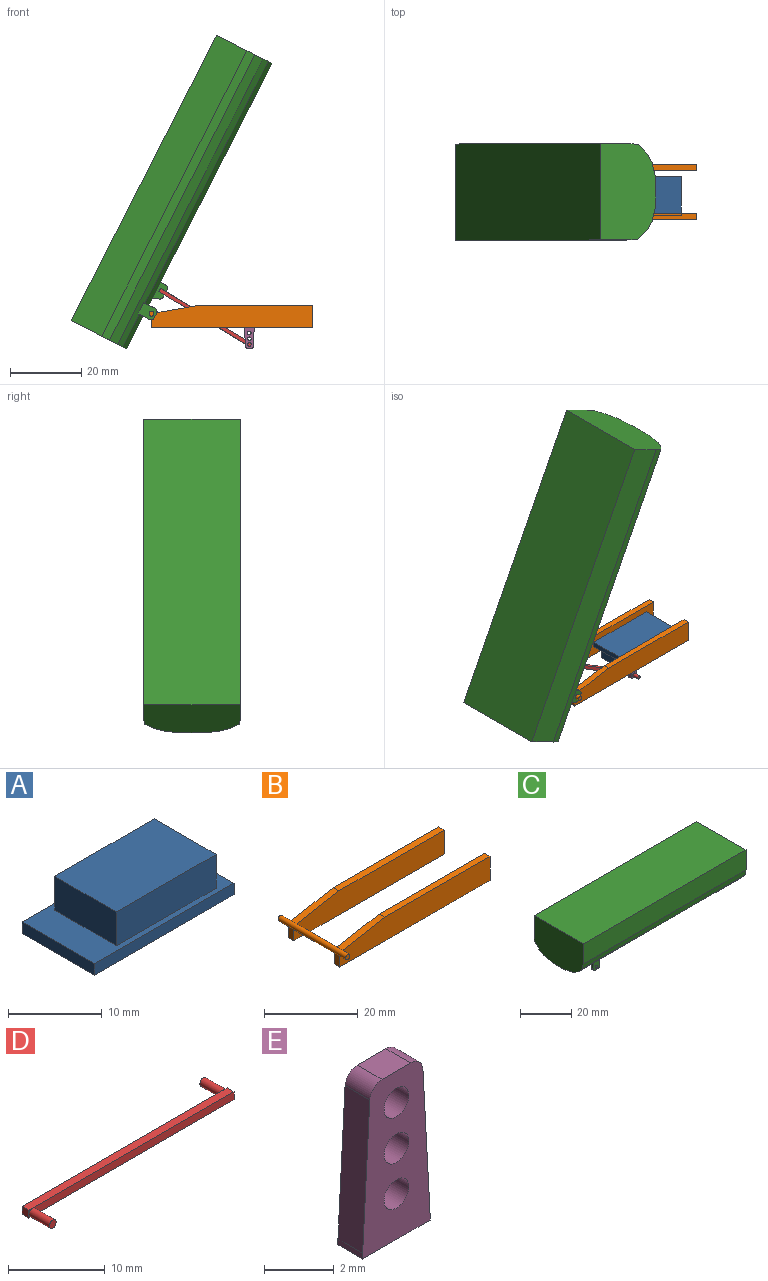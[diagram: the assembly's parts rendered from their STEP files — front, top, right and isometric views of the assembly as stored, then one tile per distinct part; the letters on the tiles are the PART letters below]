
ASSEMBLY  parts=5 mates=5
PART A: 11 faces, bbox 21x10.9x5.9 mm
  f0: plane 21x10.9mm, normal (0,0,1), area 89.4mm2, adj f1,f3,f4,f5,f6,f7,f8,f9
  f1: plane 10.9x1.5mm, normal (-1,0,0), area 16.3mm2, adj f0,f2,f4,f5
  f2: plane 21x10.9mm, normal (0,0,-1), area 228.9mm2, adj f1,f3,f4,f5
  f3: plane 10.9x1.5mm, normal (1,0,0), area 16.3mm2, adj f0,f2,f4,f5
  f4: plane 21x1.5mm, normal (0,1,0), area 31.5mm2, adj f0,f1,f2,f3
  f5: plane 21x1.5mm, normal (0,-1,0), area 31.5mm2, adj f0,f1,f2,f3
  f6: plane 15x4.4mm, normal (0,1,0), area 66mm2, adj f0,f7,f9,f10
  f7: plane 9.3x4.4mm, normal (-1,0,0), area 40.9mm2, adj f0,f6,f8,f10
  f8: plane 15x4.4mm, normal (0,-1,0), area 66mm2, adj f0,f7,f9,f10
  f9: plane 9.3x4.4mm, normal (1,0,0), area 40.9mm2, adj f0,f6,f8,f10
  f10: plane 15x9.3mm, normal (0,0,1), area 139.5mm2, adj f6,f7,f8,f9
PART B: 17 faces, bbox 46.1x20.4x6.3 mm
  f0: plane 3.18x1.7mm, normal (-1,0,0), area 5.4mm2, adj f1,f5,f6,f14
  f1: plane 45.4x1.7mm, normal (0,0,-1), area 77.2mm2, adj f0,f2,f5,f6
  f2: plane 6.25x1.7mm, normal (1,0,0), area 10.6mm2, adj f1,f3,f5,f6
  f3: plane 31.8x1.7mm, normal (0,0,1), area 54.1mm2, adj f2,f4,f5,f6
  f4: plane 12.94x2.28mm, normal (-0.17,0,0.98), area 22.3mm2, adj f3,f5,f6,f14
  f5: plane 45.4x6.25mm, normal (0,-1,0), area 267mm2, adj f0,f1,f2,f3,f4,f14
  f6: plane 45.4x6.25mm, normal (0,1,0), area 267mm2, adj f0,f1,f2,f3,f4,f14
  f7: plane 3.18x1.7mm, normal (-1,0,0), area 5.4mm2, adj f8,f12,f13,f14
  f8: plane 45.4x1.7mm, normal (0,0,-1), area 77.2mm2, adj f7,f9,f12,f13
  f9: plane 6.25x1.7mm, normal (1,0,0), area 10.6mm2, adj f8,f10,f12,f13
  f10: plane 31.8x1.7mm, normal (0,0,1), area 54.1mm2, adj f9,f11,f12,f13
  f11: plane 12.94x2.28mm, normal (-0.17,0,0.98), area 22.3mm2, adj f10,f12,f13,f14
  f12: plane 45.4x6.25mm, normal (0,-1,0), area 267mm2, adj f7,f8,f9,f10,f11,f14
  f13: plane 45.4x6.25mm, normal (0,1,0), area 267mm2, adj f7,f8,f9,f10,f11,f14
  f14: cylinder r=0.68mm len=20.4mm, axis (0,-1,0), area 82.5mm2, adj f0,f4,f5,f6,f7,f11,f12,f13
  f15: plane 1.35x1.35mm, normal (0,1,0), area 1.4mm2, adj f14
  f16: plane 1.35x1.35mm, normal (0,-1,0), area 1.4mm2, adj f14
PART C: 38 faces, bbox 90.1x27.1x20.5 mm
  f0: plane 90.1x7mm, normal (0,0,-1), area 620.7mm2, adj f1,f3,f12,f13,f30,f31,f32,f33
  f1: plane 90.1x4.85mm, normal (0,0.25,-0.97), area 448.7mm2, adj f0,f2,f12,f13,f22,f23,f25
  f2: plane 90.1x2.53mm, normal (0,0.54,-0.84), area 267.4mm2, adj f1,f11,f12,f13,f23,f24,f25
  f3: plane 90.1x4.85mm, normal (0,-0.25,-0.97), area 448.4mm2, adj f0,f4,f12,f13,f15,f16,f17
  f4: plane 90.1x2.53mm, normal (0,-0.54,-0.84), area 267.7mm2, adj f3,f5,f12,f13,f14,f15,f17
  f5: plane 90.1x2.58mm, normal (0,-0.74,-0.67), area 315.3mm2, adj f4,f6,f12,f13
  f6: plane 90.1x2.48mm, normal (0,-0.99,-0.13), area 225.2mm2, adj f5,f7,f12,f13
  f7: plane 90.1x9.6mm, normal (0,-1,0), area 865mm2, adj f6,f8,f12,f13
  f8: plane 90.1x27.13mm, normal (0,0,1), area 2444.4mm2, adj f7,f9,f12,f13
  f9: plane 90.1x9.6mm, normal (0,1,0), area 865mm2, adj f8,f10,f12,f13
  f10: plane 90.1x2.48mm, normal (0,0.99,-0.13), area 225.2mm2, adj f9,f11,f12,f13
  f11: plane 90.1x2.58mm, normal (0,0.74,-0.67), area 315.3mm2, adj f2,f10,f12,f13
  f12: plane 27.13x17.5mm, normal (1,0,0), area 434.7mm2, adj f0,f1,f2,f3,f4,f5,f6,f7
  f13: plane 27.13x17.5mm, normal (-1,0,0), area 434.7mm2, adj f0,f1,f2,f3,f4,f5,f6,f7
  f14: plane 4.62x3.5mm, normal (0,-1,0), area 14.2mm2, adj f4,f15,f17,f18,f19,f20,f21
  f15: plane 3.62x1.2mm, normal (-1,0,0), area 4mm2, adj f3,f4,f14,f16,f20
  f16: plane 4.08x3.5mm, normal (0,1,0), area 12.3mm2, adj f3,f15,f17,f18,f19,f20,f21
  f17: plane 3.62x1.2mm, normal (1,0,0), area 4mm2, adj f3,f4,f14,f16,f21
  f18: plane 1.5x1.2mm, normal (0,0,-1), area 1.8mm2, adj f14,f16,f20,f21
  f19: cylinder r=0.7mm len=1.4mm, axis (0,-1,0), area 5.3mm2, adj f14,f16
  f20: cylinder r=1mm len=1.2mm, axis (0,-1,0), area 1.9mm2, adj f14,f15,f16,f18
  f21: cylinder r=1mm len=1.2mm, axis (0,1,0), area 1.9mm2, adj f14,f16,f17,f18
  f22: plane 4.1x3.5mm, normal (0,-1,0), area 12.4mm2, adj f1,f23,f25,f26,f27,f28,f29
  f23: plane 3.67x1.2mm, normal (-1,0,0), area 4mm2, adj f1,f2,f22,f24,f29
  f24: plane 4.67x3.5mm, normal (0,1,0), area 14.4mm2, adj f2,f23,f25,f26,f27,f28,f29
  f25: plane 3.67x1.2mm, normal (1,0,0), area 4mm2, adj f1,f2,f22,f24,f28
  f26: plane 1.5x1.2mm, normal (0,0,-1), area 1.8mm2, adj f22,f24,f28,f29
  f27: cylinder r=0.7mm len=1.4mm, axis (0,-1,0), area 5.3mm2, adj f22,f24
  f28: cylinder r=1mm len=1.2mm, axis (0,1,0), area 1.9mm2, adj f22,f24,f25,f26
  f29: cylinder r=1mm len=1.2mm, axis (0,-1,0), area 1.9mm2, adj f22,f23,f24,f26
  f30: plane 5x2.6mm, normal (0,-1,0), area 10.7mm2, adj f0,f31,f33,f34,f35,f36,f37
  f31: plane 2x1.94mm, normal (-0.94,0,-0.34), area 4.1mm2, adj f0,f30,f32,f36
  f32: plane 5x2.6mm, normal (0,1,0), area 10.7mm2, adj f0,f31,f33,f34,f35,f36,f37
  f33: plane 2x1.6mm, normal (1,0,0), area 3.2mm2, adj f0,f30,f32,f37
  f34: plane 2.35x2mm, normal (0,0,-1), area 4.7mm2, adj f30,f32,f36,f37
  f35: cylinder r=0.5mm len=2mm, axis (0,-1,0), area 6.3mm2, adj f30,f32
  f36: cylinder r=1mm len=2mm, axis (0,1,0), area 2.4mm2, adj f30,f31,f32,f34
  f37: cylinder r=1mm len=2mm, axis (0,1,0), area 3.1mm2, adj f30,f32,f33,f34
PART D: 14 faces, bbox 30x7x1 mm
  f0: plane 0.5x0.5mm, normal (0,1,0), area 0.1mm2, adj f4,f7,f12
  f1: plane 0.5x0.5mm, normal (0,1,0), area 0.1mm2, adj f6,f7,f12
  f2: plane 29.5x1mm, normal (0,-1,0), area 29.1mm2, adj f4,f6,f7,f10
  f3: plane 0.5x0.5mm, normal (0,-1,0), area 0.1mm2, adj f4,f5,f10
  f4: plane 30x1mm, normal (0,0,1), area 30mm2, adj f0,f2,f3,f5,f7,f9
  f5: plane 1x1mm, normal (-1,0,0), area 1mm2, adj f3,f4,f6,f8,f9
  f6: plane 30x1mm, normal (0,0,-1), area 30mm2, adj f1,f2,f5,f7,f8,f9
  f7: plane 1x1mm, normal (1,0,0), area 1mm2, adj f0,f1,f2,f4,f6
  f8: plane 0.5x0.5mm, normal (0,-1,0), area 0.1mm2, adj f5,f6,f10
  f9: plane 29.5x1mm, normal (0,1,0), area 29.1mm2, adj f4,f5,f6,f12
  f10: cylinder r=0.5mm len=3mm, axis (0,1,0), area 9.4mm2, adj f2,f3,f8,f11
  f11: plane 1x1mm, normal (0,-1,0), area 0.8mm2, adj f10
  f12: cylinder r=0.5mm len=3mm, axis (0,-1,0), area 9.4mm2, adj f0,f1,f9,f13
  f13: plane 1x1mm, normal (0,1,0), area 0.8mm2, adj f12
PART E: 13 faces, bbox 2.7x1x5.9 mm
  f0: plane 1x0.2mm, normal (-1,0,0), area 0.2mm2, adj f1,f7,f8,f9
  f1: plane 2.73x1mm, normal (0,0,-1), area 2.7mm2, adj f0,f2,f8,f9
  f2: plane 1x0.2mm, normal (1,0,0), area 0.2mm2, adj f1,f3,f8,f9
  f3: plane 5.23x1mm, normal (1,0,0.06), area 5.2mm2, adj f2,f4,f8,f9
  f4: cylinder r=0.5mm len=1mm, axis (0,-1,0), area 0.8mm2, adj f3,f5,f8,f9
  f5: plane 1.15x1mm, normal (0,0,1), area 1.2mm2, adj f4,f6,f8,f9
  f6: cylinder r=0.5mm len=1mm, axis (0,-1,0), area 0.8mm2, adj f5,f7,f8,f9
  f7: plane 5.23x1mm, normal (-1,0,0.06), area 5.2mm2, adj f0,f6,f8,f9
  f8: plane 5.9x2.73mm, normal (0,1,0), area 11.9mm2, adj f0,f1,f2,f3,f4,f5,f6,f7
  f9: plane 5.9x2.73mm, normal (0,-1,0), area 11.9mm2, adj f0,f1,f2,f3,f4,f5,f6,f7
  f10: cylinder r=0.5mm len=1mm, axis (0,-1,0), area 3.1mm2, adj f8,f9
  f11: cylinder r=0.5mm len=1mm, axis (0,-1,0), area 3.1mm2, adj f8,f9
  f12: cylinder r=0.5mm len=1mm, axis (0,-1,0), area 3.1mm2, adj f8,f9
PLACE A rot(axis=(0,1,0),180deg) t=(54.69,16.31,12.16)mm fixed
PLACE B t=(0,16.7,0)mm fixed
PLACE C rot(axis=(0,-1,0),63deg) t=(3.43,16.69,2.1)mm
PLACE D rot(axis=(-0.96,0,0.27),180deg) t=(11.98,19.77,71.08)mm
PLACE E rot(axis=(0,-1,0),180deg) t=(48.38,18.07,12.16)mm
MATE revolute C.f19 <-> B.f14  axis (0,-1,0) through (0,13.8,3.85)mm
MATE parallel E.f1 <-> A.f10  axis (0,0,1) through (27.52,19.27,0)mm
MATE revolute D.f10 <-> C.f35  axis (0,1,0) through (2.76,23.77,10.31)mm
MATE planar A.f10 <-> E.f1  axis (0,0,-1) through (29.5,21.65,0)mm
MATE revolute D.f12 <-> E.f12  axis (0,1,0) through (27.52,19.77,-4.8)mm
